# Revit family: Urinal-Vitra_ArkitektSeries_6202B003-0198
name_source: partatom
category: Plumbing Fixtures
revit_build: Autodesk Revit 2017 (Build: 20160225_1515(x64)
units: mm (PartAtom-declared; Revit-internal decimal feet)

## family parameters
Cut with Voids When Loaded = No
Host = Face
OmniClass Number = 23.45.05.21.11.21
OmniClass Title = Urinals
Part Type = Normal
Room Calculation Point = No
Round Connector Dimension = Use Diameter
Shared = Yes

## types (4) — shared parameters
BIMobject category = Urinals
CW Connection = Yes
Default Elevation = 650 mm  [stored 2.13255 ft]
Description = VitrA Arkitekt Top Water Inlet
Design country = Turkey
HW Connection = No
IFC Classification = Sanitary Terminal
Installation instructions = https://cdn.vitra.com.tr
Main Material = Ceramic
Manufacturer = Vitra
Manufacturer name = Vitra
Masterformat 2014 Code = 22 41 13.16
Masterformat 2014 Description = Residential Urinals
MountingType = Wall Mounted
NBS Referans Code = 31-93
NBS Referans Description = Urinal And Wc Fittings
Nominal Depth = 310 mm  [stored 1.01706 ft]
NominalHeight = 565 mm  [stored 1.85367 ft]
NominalWidth = 315 mm  [stored 1.03346 ft]
OmniClass Code = 23-31 21 00
OmniClass Description = Urinals
Product certification = https://vitraglobal.com
Product data url = https://www.vitraglobal.com
Product family = Wall Mounted Urinal
Product group = Arkitekt
Technical description = https://www.vitraglobal.com
UNSPSC Code = 30181506
URL = https://www.vitra.com.tr
Uniclass 1.4 Code = L721
Uniclass 1.4 Description = Sanitary equipment
Uniclass 2.0 Code = PR-31-93
Uniclass 2.0 Description = Urinal And Wc Fittings
Uniclass 2015 Code = Pr_40_20_93
Uniclass 2015 Name = Urinal and WC fittings
Uniformat II Code = D2010
Uniformat II Description = Plumbing Fixtures
Vent Connection = No
Warranty Period (Year) = 10 Years
Waste Connection = Yes
Weight Net (kg) = 14,375
Youtube = https://www.youtube.com
zero-valued in all types: Cost

## per-type parameters (varying)
| type | Article No. (default) | Color | Model | Product SKU | Secondary Material |
| Urinal_Vitra_Arkitekt_6202B003-0198 | 6202B003-0198 | White | 6202B003-0198 | 6202B003-0198 | Ceramic-White |
| Urinal_Vitra_Arkitekt_6202B095-0198 | 6202B095-0198 | Pergamon | 6202B095-0198 | 6202B095-0198 | Ceramic-Pergamon |
| Urinal_Vitra_Arkitekt_6202B403-0198 | 6202B403-0198 | White | 6202B403-0198 | 6202B403-0198 | Ceramic-White |
| Urinal_Vitra_Arkitekt_6202L003D0202 | 6202L003D0202 | White | 6202L003D0202 | 6202L003D0202 | Ceramic-White |

note: [stored X ft] marks values corroborated as IEEE doubles in the binary element streams (Revit-internal decimal feet)

## geometry (parser evidence)
native form markers: Sweep x3
no freeform markers — native parametric forms only
